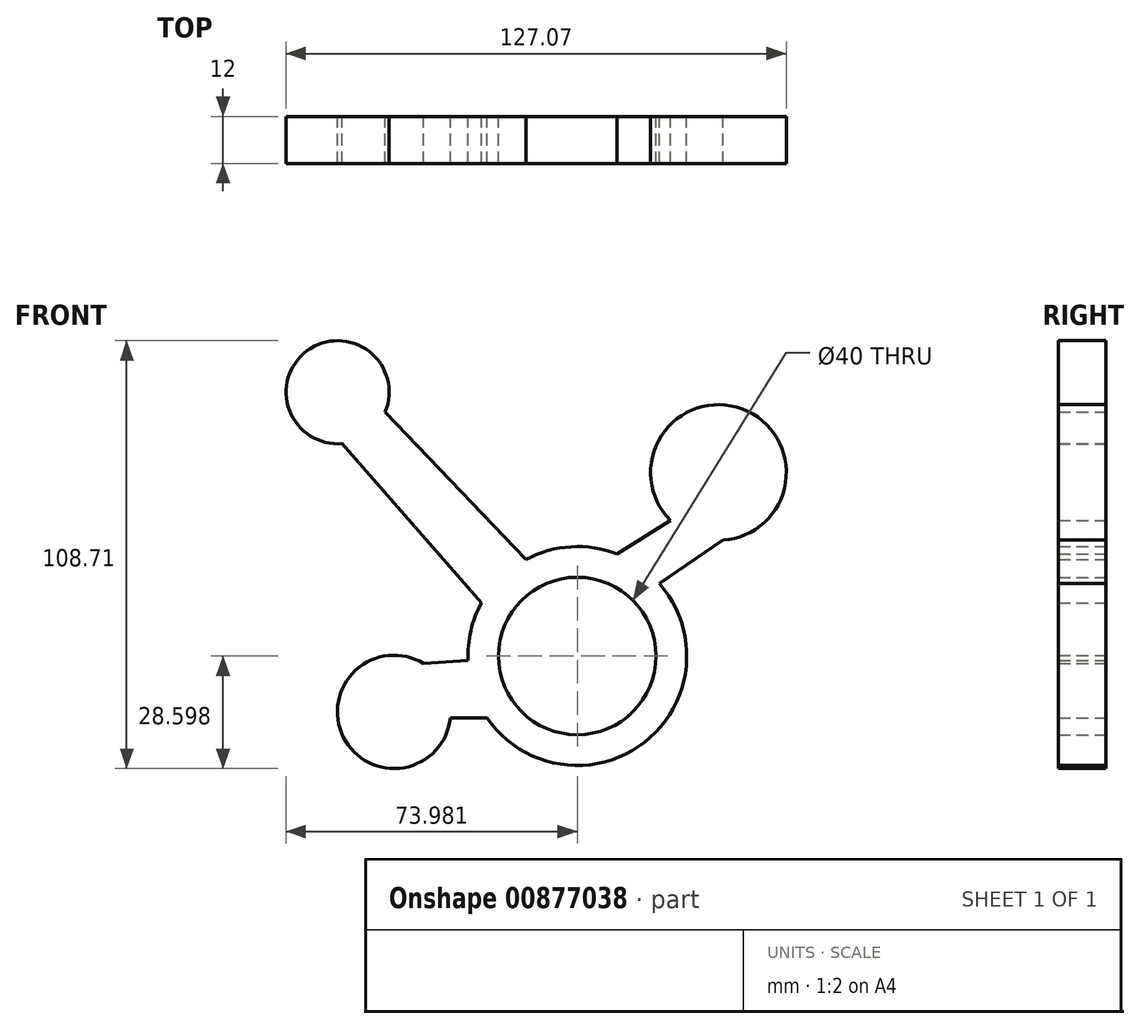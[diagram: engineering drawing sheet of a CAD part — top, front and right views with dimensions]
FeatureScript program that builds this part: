
annotation { "Feature Type Name" : "Feature", "Feature Type Description" : "" }
export const myFeature = defineFeature(function(context is Context, id is Id, definition is map)
    precondition{}
    {
        {
            var Q0;
            Q0=qCreatedBy(makeId("Front.planeOp"),FACE);
            var sketch = newSketch(context, id + "F0", { "sketchPlane" : qUnion([Q0])});
            skCircle(sketch, "E0", {"center": v(3.65, 68.08) * mm, "radius": 20 * mm});
            skPoint(sketch, "E1.end.orphan", {"position": v(-49.29, 56.9) * mm});
            skCircle(sketch, "E2", {"center": v(-57.24, 135.1) * mm, "radius": 13.1 * mm});
            skCircle(sketch, "E3", {"center": v(39.5, 114.7) * mm, "radius": 17.24 * mm});
            skCircle(sketch, "E4", {"center": v(-42.9, 53.88) * mm, "radius": 14.4 * mm});
            skLineSegment(sketch, "E5", {"start": v(-56.05, 122.06) * mm, "end": v(-20.67, 81.54) * mm});
            skLineSegment(sketch, "E6", {"start": v(-20.67, 81.54) * mm, "end": v(-56.05, 122.06) * mm});
            skLineSegment(sketch, "E7", {"start": v(-45.14, 130.09) * mm, "end": v(-9.4, 92.63) * mm});
            skLineSegment(sketch, "E8", {"start": v(27.31, 102.52) * mm, "end": v(13.78, 93.97) * mm});
            skLineSegment(sketch, "E9", {"start": v(40.65, 97.5) * mm, "end": v(24.49, 86.48) * mm});
            skLineSegment(sketch, "E10", {"start": v(-24.13, 66.95) * mm, "end": v(-35.43, 66.2) * mm});
            skLineSegment(sketch, "E11", {"start": v(-35.43, 66.2) * mm, "end": v(-30.25, 60.76) * mm});
            skLineSegment(sketch, "E12", {"start": v(-28.58, 52.34) * mm, "end": v(-19.27, 52.34) * mm});
            skCircle(sketch, "E13", {"center": v(3.65, 68.08) * mm, "radius": 27.8 * mm});
            skSolve(sketch);
        }
        {
            var Q0;
            Q0 = qSketchRegion(id + "F0", true);
            extrude(context, id + "F1", {"entities" : qUnion([Q0]), "depth" : 12 * mm, "offsetDistance" : 25.4 * mm});
        }
    });
